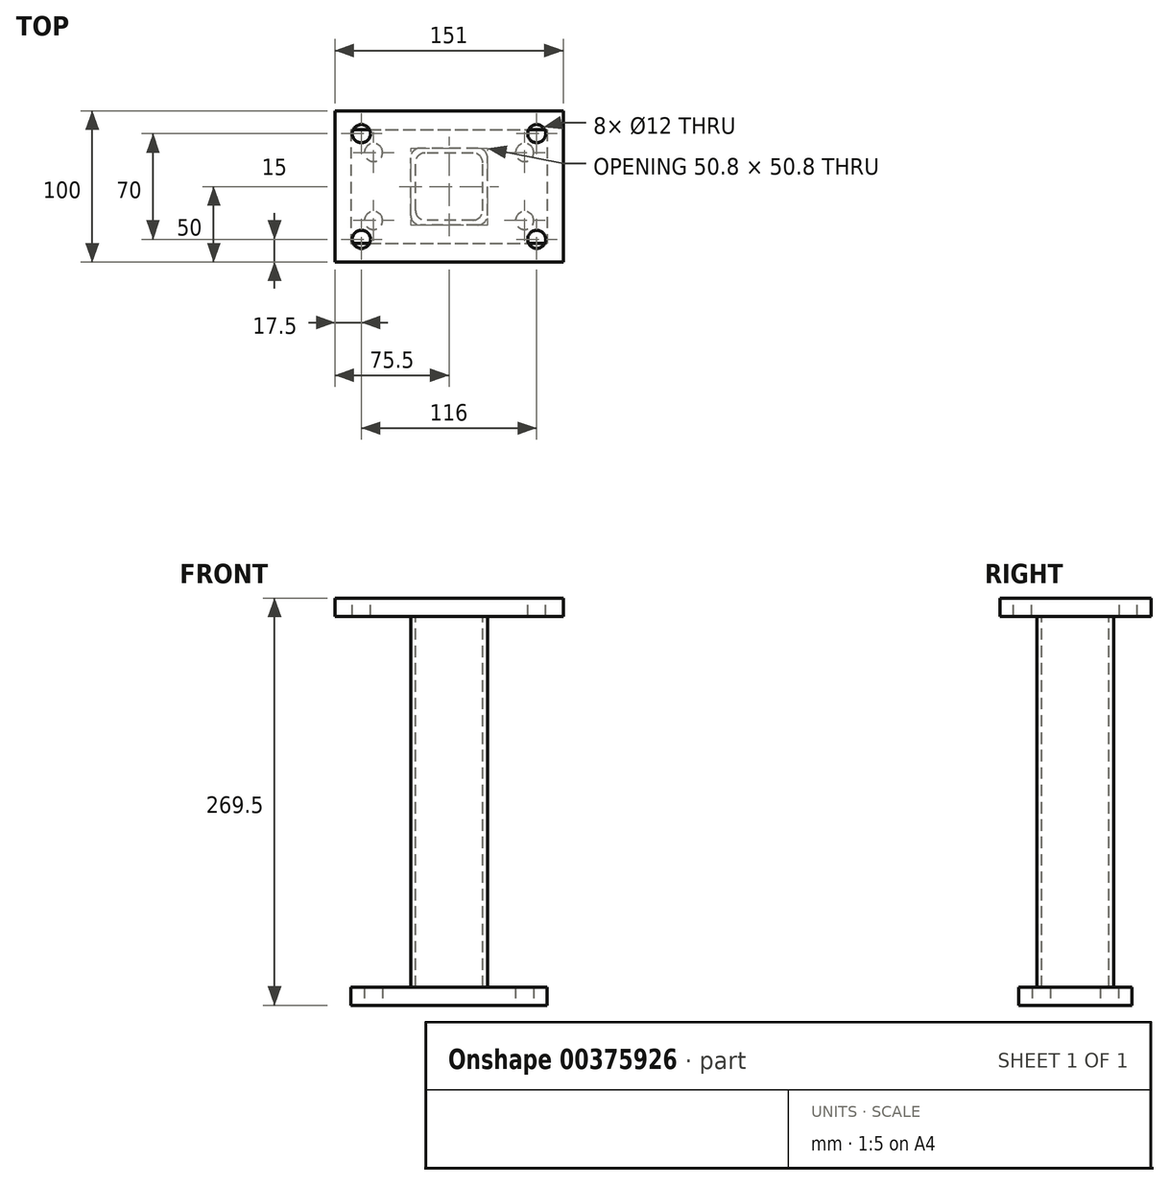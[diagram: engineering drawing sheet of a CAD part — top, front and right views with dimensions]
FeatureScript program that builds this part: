
annotation { "Feature Type Name" : "Feature", "Feature Type Description" : "" }
export const myFeature = defineFeature(function(context is Context, id is Id, definition is map)
    precondition{}
    {
        {
            var Q0;
            Q0=qCreatedBy(makeId("Top.planeOp"),FACE);
            var sketch = newSketch(context, id + "F0", { "sketchPlane" : qUnion([Q0])});
            skLineSegment(sketch, "E0.bottom", {"start": v(0, 0) * mm, "end": v(151, 0) * mm});
            skLineSegment(sketch, "E0.top", {"start": v(0, 100) * mm, "end": v(151, 100) * mm});
            skLineSegment(sketch, "E0.left", {"start": v(0, 0) * mm, "end": v(0, 100) * mm});
            skLineSegment(sketch, "E0.right", {"start": v(151, 0) * mm, "end": v(151, 100) * mm});
            skSolve(sketch);
        }
        {
            var Q0;
            Q0=makeQuery(id+"F0.imprint","IMPRINT",FACE,{"disambiguationData":[TD([[makeQuery(id+"F0.imprint","IMPRINT",EDGE,{"derivedFrom":sQuery(id+"F0.wireOp",EDGE,"E0.bottom")}),1.0]])]});
            extrude(context, id + "F1", {"entities" : qUnion([Q0]), "depth" : 12 * mm});
        }
        {
            var Q0;
            Q0=makeQuery(id+"F1.opExtrude","CAP_FACE",FACE,{"disambiguationData":[OSD([sQuery(id+"F0.wireOp",EDGE,"E0.bottom"),sQuery(id+"F0.wireOp",EDGE,"E0.top"),sQuery(id+"F0.wireOp",EDGE,"E0.left"),sQuery(id+"F0.wireOp",EDGE,"E0.right")])],"isStart":true});
            var sketch = newSketch(context, id + "F2", { "sketchPlane" : qUnion([Q0])});
            skLineSegment(sketch, "E1.bottom", {"start": v(94.55, -24.6) * mm, "end": v(56.45, -24.6) * mm});
            skLineSegment(sketch, "E1.top", {"start": v(94.55, -75.4) * mm, "end": v(56.45, -75.4) * mm});
            skLineSegment(sketch, "E1.left", {"start": v(100.9, -30.95) * mm, "end": v(100.9, -69.05) * mm});
            skLineSegment(sketch, "E1.right", {"start": v(50.1, -30.95) * mm, "end": v(50.1, -69.05) * mm});
            skPoint(sketch, "E1.middle", {"position": v(75.5, -50) * mm});
            skPoint(sketch, "E1.middle.positionSnap0", {"position": v(75.5, -100) * mm});
            skPoint(sketch, "E1.middle.positionSnap1", {"position": v(0, -50) * mm});
            skPoint(sketch, "E1.centerSnap0", {"position": v(75.5, -100) * mm});
            skPoint(sketch, "E1.centerSnap1", {"position": v(0, -50) * mm});
            skLineSegment(sketch, "E2.bottom", {"start": v(91.37, -27.77) * mm, "end": v(59.62, -27.77) * mm});
            skLineSegment(sketch, "E2.top", {"start": v(91.37, -72.22) * mm, "end": v(59.62, -72.22) * mm});
            skLineSegment(sketch, "E2.left", {"start": v(97.72, -34.12) * mm, "end": v(97.72, -65.87) * mm});
            skLineSegment(sketch, "E2.right", {"start": v(53.27, -34.12) * mm, "end": v(53.27, -65.87) * mm});
            skPoint(sketch, "E3.visualSharp", {"position": v(100.9, -24.6) * mm});
            skArc(sketch, "E3.filletArc", {"start": v(100.9, -30.95) * mm, "mid": v(99.04, -26.46) * mm, "end": v(94.55, -24.6) * mm});
            skPoint(sketch, "E4.visualSharp", {"position": v(100.9, -75.4) * mm});
            skArc(sketch, "E4.filletArc", {"start": v(94.55, -75.4) * mm, "mid": v(99.04, -73.54) * mm, "end": v(100.9, -69.05) * mm});
            skPoint(sketch, "E5.visualSharp", {"position": v(50.1, -75.4) * mm});
            skArc(sketch, "E5.filletArc", {"start": v(50.1, -69.05) * mm, "mid": v(51.96, -73.54) * mm, "end": v(56.45, -75.4) * mm});
            skPoint(sketch, "E6.visualSharp", {"position": v(50.1, -24.6) * mm});
            skArc(sketch, "E6.filletArc", {"start": v(56.45, -24.6) * mm, "mid": v(51.96, -26.46) * mm, "end": v(50.1, -30.95) * mm});
            skPoint(sketch, "E7.visualSharp", {"position": v(53.27, -27.77) * mm});
            skArc(sketch, "E7.filletArc", {"start": v(59.62, -27.77) * mm, "mid": v(55.13, -29.63) * mm, "end": v(53.27, -34.12) * mm});
            skPoint(sketch, "E8.visualSharp", {"position": v(53.27, -72.22) * mm});
            skArc(sketch, "E8.filletArc", {"start": v(53.27, -65.87) * mm, "mid": v(55.13, -70.37) * mm, "end": v(59.62, -72.23) * mm});
            skPoint(sketch, "E9.visualSharp", {"position": v(97.72, -72.22) * mm});
            skArc(sketch, "E9.filletArc", {"start": v(91.37, -72.22) * mm, "mid": v(95.87, -70.37) * mm, "end": v(97.72, -65.87) * mm});
            skPoint(sketch, "E10.visualSharp", {"position": v(97.72, -27.77) * mm});
            skArc(sketch, "E10.filletArc", {"start": v(97.72, -34.12) * mm, "mid": v(95.87, -29.63) * mm, "end": v(91.37, -27.78) * mm});
            skSolve(sketch);
        }
        {
            var Q0;
            Q0=makeQuery(id+"F2.imprint","IMPRINT",FACE,{"disambiguationData":[TD([[makeQuery(id+"F2.imprint","IMPRINT",EDGE,{"derivedFrom":sQuery(id+"F2.wireOp",EDGE,"E1.bottom")}),1.0]])]});
            extrude(context, id + "F3", {"entities" : qUnion([Q0]), "operationType" : NewBodyOperationType.ADD, "depth" : 245.5 * mm});
        }
        {
            var Q0;
            Q0=makeQuery(id+"F1.opExtrude","CAP_FACE",FACE,{"disambiguationData":[OSD([sQuery(id+"F0.wireOp",EDGE,"E0.bottom"),sQuery(id+"F0.wireOp",EDGE,"E0.top"),sQuery(id+"F0.wireOp",EDGE,"E0.left"),sQuery(id+"F0.wireOp",EDGE,"E0.right")])],"isStart":false});
            var sketch = newSketch(context, id + "F4", { "sketchPlane" : qUnion([Q0])});
            skLineSegment(sketch, "E11", {"start": v(151, 0) * mm, "end": v(133.5, 0) * mm, "construction": true});
            skLineSegment(sketch, "E12", {"start": v(133.5, 0) * mm, "end": v(133.5, 15) * mm, "construction": true});
            skLineSegment(sketch, "E13", {"start": v(151, 50) * mm, "end": v(0, 50) * mm, "construction": true});
            skLineSegment(sketch, "E14", {"start": v(75.5, 100) * mm, "end": v(75.5, 0) * mm, "construction": true});
            skLineSegment(sketch, "E15.MirrorCS", {"start": v(133.5, 100) * mm, "end": v(133.5, 85) * mm, "construction": true});
            skLineSegment(sketch, "E16.MirrorCS", {"start": v(151, 100) * mm, "end": v(133.5, 100) * mm, "construction": true});
            skLineSegment(sketch, "E17.MirrorCS", {"start": v(17.5, 100) * mm, "end": v(17.5, 85) * mm, "construction": true});
            skLineSegment(sketch, "E18.MirrorCS", {"start": v(0, 100) * mm, "end": v(17.5, 100) * mm, "construction": true});
            skLineSegment(sketch, "E19.MirrorCS", {"start": v(17.5, 0) * mm, "end": v(17.5, 15) * mm, "construction": true});
            skLineSegment(sketch, "E20.MirrorCS", {"start": v(0, 0) * mm, "end": v(17.5, 0) * mm, "construction": true});
            skSolve(sketch);
        }
        {
            var Q0;
            Q0=sQuery(id+"F4.wireOp",VERTEX,"E17.MirrorCS.end");
            var Q1;
            Q1=sQuery(id+"F4.wireOp",VERTEX,"E15.MirrorCS.end");
            var Q2;
            Q2=sQuery(id+"F4.wireOp",VERTEX,"E12.end");
            var Q3;
            Q3=sQuery(id+"F4.wireOp",VERTEX,"E19.MirrorCS.end");
            var Q4;
            Q4=makeQuery(id+"F1.opExtrude","SWEPT_BODY",BODY,{"disambiguationData":[OSD([sQuery(id+"F0.wireOp",EDGE,"E0.bottom"),sQuery(id+"F0.wireOp",EDGE,"E0.top"),sQuery(id+"F0.wireOp",EDGE,"E0.left"),sQuery(id+"F0.wireOp",EDGE,"E0.right")])]});
            hole(context, id + "F5", {"style" : HoleStyle.SIMPLE, "endStyle" : HoleEndStyle.BLIND, "holeDiameter" : 12 * mm, "holeDepth" : 12 * mm, "isTappedThrough" : true, "tappedDepth" : 12 * mm, "tapClearance" : 3, "locations" : qUnion([Q0, Q1, Q2, Q3]), "scope" : qUnion([Q4])});
        }
        {
            var Q0;
            Q0=makeQuery(id+"F3.opExtrude","CAP_FACE",FACE,{"disambiguationData":[OSD([sQuery(id+"F2.wireOp",EDGE,"E1.bottom"),sQuery(id+"F2.wireOp",EDGE,"E1.top"),sQuery(id+"F2.wireOp",EDGE,"E1.left"),sQuery(id+"F2.wireOp",EDGE,"E1.right"),sQuery(id+"F2.wireOp",EDGE,"E2.bottom"),sQuery(id+"F2.wireOp",EDGE,"E2.top"),sQuery(id+"F2.wireOp",EDGE,"E2.left"),sQuery(id+"F2.wireOp",EDGE,"E2.right"),sQuery(id+"F2.wireOp",EDGE,"E3.filletArc"),sQuery(id+"F2.wireOp",EDGE,"E4.filletArc"),sQuery(id+"F2.wireOp",EDGE,"E5.filletArc"),sQuery(id+"F2.wireOp",EDGE,"E6.filletArc"),sQuery(id+"F2.wireOp",EDGE,"E7.filletArc"),sQuery(id+"F2.wireOp",EDGE,"E8.filletArc"),sQuery(id+"F2.wireOp",EDGE,"E9.filletArc"),sQuery(id+"F2.wireOp",EDGE,"E10.filletArc")])],"isStart":false});
            var sketch = newSketch(context, id + "F6", { "sketchPlane" : qUnion([Q0])});
            skLineSegment(sketch, "E21.bottom", {"start": v(10.5, -87.5) * mm, "end": v(140.5, -87.5) * mm});
            skLineSegment(sketch, "E21.top", {"start": v(10.5, -12.5) * mm, "end": v(140.5, -12.5) * mm});
            skLineSegment(sketch, "E21.left", {"start": v(10.5, -87.5) * mm, "end": v(10.5, -12.5) * mm});
            skLineSegment(sketch, "E21.right", {"start": v(140.5, -87.5) * mm, "end": v(140.5, -12.5) * mm});
            skPoint(sketch, "E21.middle", {"position": v(75.5, -50) * mm});
            skPoint(sketch, "E21.middle.positionSnap0", {"position": v(53.27, -50) * mm});
            skPoint(sketch, "E21.middle.positionSnap1", {"position": v(75.5, -72.22) * mm});
            skPoint(sketch, "E21.centerSnap0", {"position": v(53.27, -50) * mm});
            skPoint(sketch, "E21.centerSnap1", {"position": v(75.5, -72.22) * mm});
            skSolve(sketch);
        }
        {
            var Q0;
            Q0=makeQuery(id+"F6.imprint","IMPRINT",FACE,{"disambiguationData":[TD([[makeQuery(id+"F6.imprint","IMPRINT",EDGE,{"derivedFrom":sQuery(id+"F6.wireOp",EDGE,"E21.bottom")}),1.0]])]});
            var Q1;
            Q1=makeQuery(id+"F6.imprint","IMPRINT",FACE,{"disambiguationData":[TD([[makeQuery(id+"F6.imprint","IMPRINT",EDGE,{"derivedFrom":makeQuery(id+"F3.opExtrude","CAP_EDGE",EDGE,{"disambiguationData":[OSD([sQuery(id+"F2.wireOp",EDGE,"E1.bottom")])],"isStart":false})}),1.0]])]});
            var Q2;
            Q2=makeQuery(id+"F6.imprint","IMPRINT",FACE,{"disambiguationData":[TD([[makeQuery(id+"F6.imprint","IMPRINT",EDGE,{"derivedFrom":makeQuery(id+"F3.opExtrude","CAP_EDGE",EDGE,{"disambiguationData":[OSD([sQuery(id+"F2.wireOp",EDGE,"E2.bottom")])],"isStart":false})}),1.0]])]});
            extrude(context, id + "F7", {"entities" : qUnion([Q0, Q1, Q2]), "operationType" : NewBodyOperationType.ADD, "depth" : 12 * mm});
        }
        {
            var Q0;
            Q0=makeQuery(id+"F7.opExtrude","CAP_FACE",FACE,{"disambiguationData":[OSD([sQuery(id+"F6.wireOp",EDGE,"E21.bottom"),sQuery(id+"F6.wireOp",EDGE,"E21.top"),sQuery(id+"F6.wireOp",EDGE,"E21.left"),sQuery(id+"F6.wireOp",EDGE,"E21.right")])],"isStart":false});
            var sketch = newSketch(context, id + "F8", { "sketchPlane" : qUnion([Q0])});
            skLineSegment(sketch, "E22", {"start": v(10.5, -12.5) * mm, "end": v(10.5, -27.5) * mm, "construction": true});
            skLineSegment(sketch, "E23", {"start": v(10.5, -27.5) * mm, "end": v(25.5, -27.5) * mm, "construction": true});
            skLineSegment(sketch, "E24", {"start": v(140.5, -87.5) * mm, "end": v(125.5, -87.5) * mm, "construction": true});
            skLineSegment(sketch, "E25", {"start": v(125.5, -87.5) * mm, "end": v(125.5, -72.5) * mm, "construction": true});
            skLineSegment(sketch, "E26", {"start": v(140.5, -12.5) * mm, "end": v(125.5, -12.5) * mm, "construction": true});
            skLineSegment(sketch, "E27", {"start": v(125.5, -12.5) * mm, "end": v(125.5, -27.5) * mm, "construction": true});
            skLineSegment(sketch, "E28", {"start": v(10.5, -87.5) * mm, "end": v(10.5, -72.5) * mm, "construction": true});
            skLineSegment(sketch, "E29", {"start": v(10.5, -72.5) * mm, "end": v(25.5, -72.5) * mm, "construction": true});
            skSolve(sketch);
        }
        {
            var Q0;
            Q0=sQuery(id+"F8.wireOp",VERTEX,"E23.end");
            var Q1;
            Q1=sQuery(id+"F8.wireOp",VERTEX,"E29.end");
            var Q2;
            Q2=sQuery(id+"F8.wireOp",VERTEX,"E25.end");
            var Q3;
            Q3=sQuery(id+"F8.wireOp",VERTEX,"E27.end");
            var Q4;
            Q4=makeQuery(id+"F1.opExtrude","SWEPT_BODY",BODY,{"disambiguationData":[OSD([sQuery(id+"F0.wireOp",EDGE,"E0.bottom"),sQuery(id+"F0.wireOp",EDGE,"E0.top"),sQuery(id+"F0.wireOp",EDGE,"E0.left"),sQuery(id+"F0.wireOp",EDGE,"E0.right")])]});
            hole(context, id + "F9", {"style" : HoleStyle.SIMPLE, "endStyle" : HoleEndStyle.BLIND, "holeDiameter" : 12 * mm, "holeDepth" : 12 * mm, "isTappedThrough" : true, "tappedDepth" : 12 * mm, "tapClearance" : 3, "locations" : qUnion([Q0, Q1, Q2, Q3]), "scope" : qUnion([Q4])});
        }
    });
